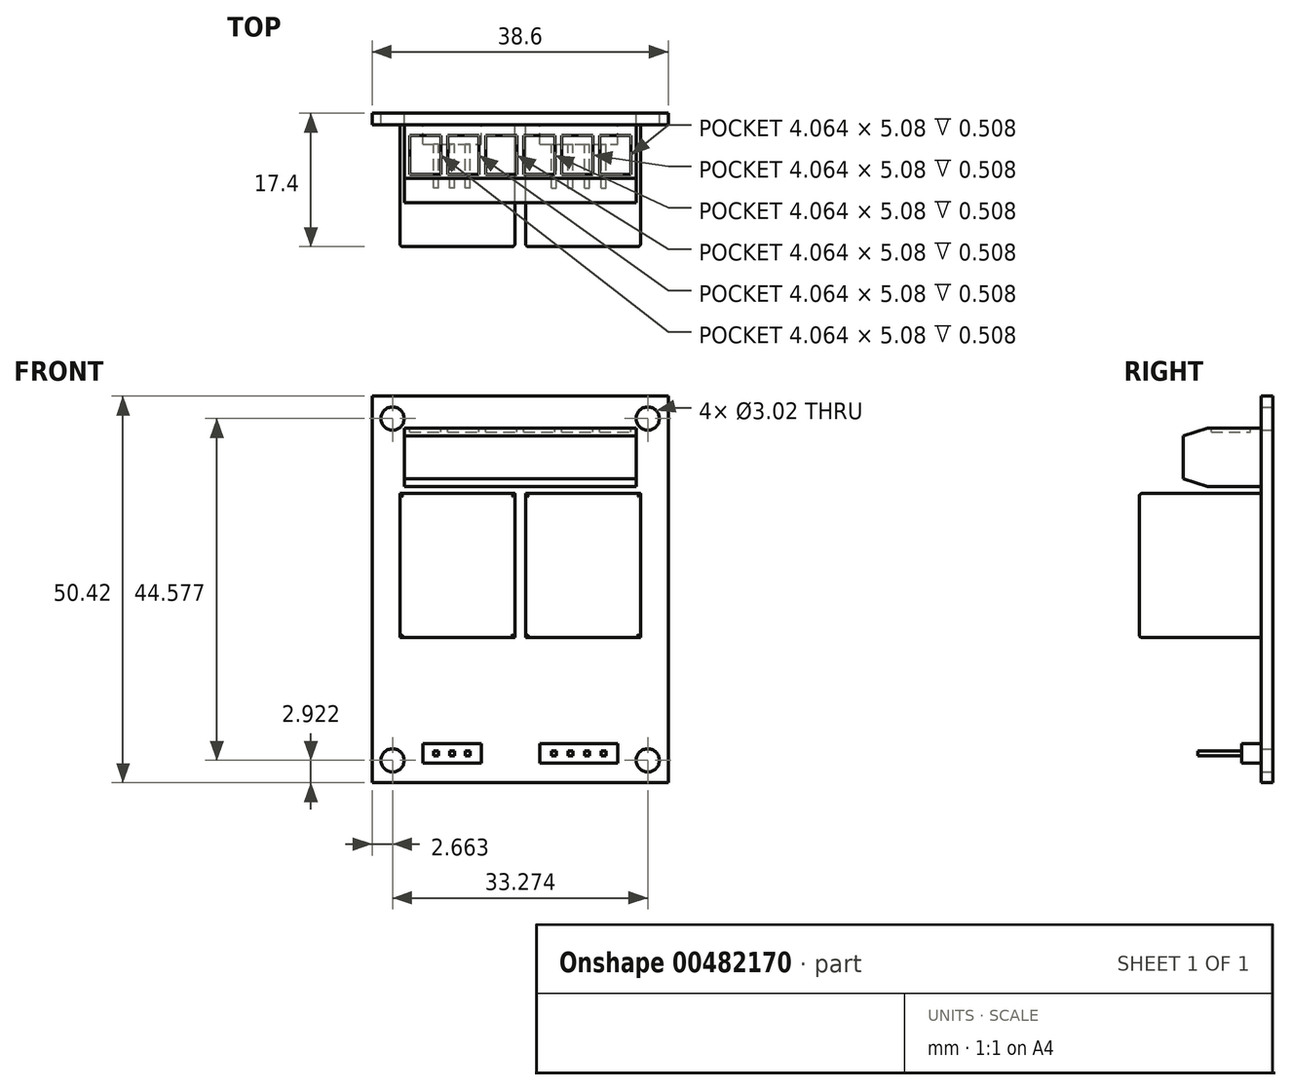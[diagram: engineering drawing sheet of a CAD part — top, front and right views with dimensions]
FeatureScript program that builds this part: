
annotation { "Feature Type Name" : "Feature", "Feature Type Description" : "" }
export const myFeature = defineFeature(function(context is Context, id is Id, definition is map)
    precondition{}
    {
        {
            var Q0;
            Q0=qCreatedBy(makeId("Front.planeOp"),FACE);
            var sketch = newSketch(context, id + "F0", { "sketchPlane" : qUnion([Q0])});
            skLineSegment(sketch, "E0.bottom", {"start": v(-19.3, 25.2) * mm, "end": v(19.3, 25.2) * mm});
            skLineSegment(sketch, "E0.top", {"start": v(-19.3, -25.2) * mm, "end": v(19.3, -25.2) * mm});
            skLineSegment(sketch, "E0.left", {"start": v(-19.3, 25.2) * mm, "end": v(-19.3, -25.2) * mm});
            skLineSegment(sketch, "E0.right", {"start": v(19.3, 25.2) * mm, "end": v(19.3, -25.2) * mm});
            skPoint(sketch, "E0.middle", {"position": v(0, 0) * mm});
            skLineSegment(sketch, "E1.bottom", {"start": v(16.64, 22.29) * mm, "end": v(-16.64, 22.29) * mm, "construction": true});
            skLineSegment(sketch, "E1.top", {"start": v(16.64, -22.29) * mm, "end": v(-16.64, -22.29) * mm, "construction": true});
            skLineSegment(sketch, "E1.left", {"start": v(16.64, 22.29) * mm, "end": v(16.64, -22.29) * mm, "construction": true});
            skLineSegment(sketch, "E1.right", {"start": v(-16.64, 22.29) * mm, "end": v(-16.64, -22.29) * mm, "construction": true});
            skCircle(sketch, "E2", {"center": v(-16.64, 22.29) * mm, "radius": 1.51 * mm});
            skCircle(sketch, "E3", {"center": v(16.64, 22.29) * mm, "radius": 1.51 * mm});
            skCircle(sketch, "E4", {"center": v(16.64, -22.29) * mm, "radius": 1.51 * mm});
            skCircle(sketch, "E5", {"center": v(-16.64, -22.29) * mm, "radius": 1.51 * mm});
            skSolve(sketch);
        }
        {
            var Q0;
            Q0 = qSketchRegion(id + "F0", true);
            extrude(context, id + "F1", {"entities" : qUnion([Q0]), "depth" : 1.52 * mm});
        }
        {
            var Q0;
            Q0=makeQuery(id+"F1.opExtrude","CAP_FACE",FACE,{"disambiguationData":[OSD([sQuery(id+"F0.wireOp",EDGE,"E0.bottom"),sQuery(id+"F0.wireOp",EDGE,"E0.top"),sQuery(id+"F0.wireOp",EDGE,"E0.left"),sQuery(id+"F0.wireOp",EDGE,"E0.right"),sQuery(id+"F0.wireOp",EDGE,"E2"),sQuery(id+"F0.wireOp",EDGE,"E3"),sQuery(id+"F0.wireOp",EDGE,"E4"),sQuery(id+"F0.wireOp",EDGE,"E5")])],"isStart":false});
            var sketch = newSketch(context, id + "F2", { "sketchPlane" : qUnion([Q0])});
            skLineSegment(sketch, "E6.bottom", {"start": v(-15.68, -6.29) * mm, "end": v(-0.7, -6.29) * mm});
            skLineSegment(sketch, "E6.top", {"start": v(-15.68, 12.5) * mm, "end": v(-0.7, 12.5) * mm});
            skLineSegment(sketch, "E6.left", {"start": v(-15.68, -6.29) * mm, "end": v(-15.68, 12.5) * mm});
            skLineSegment(sketch, "E6.right", {"start": v(-0.7, -6.29) * mm, "end": v(-0.7, 12.5) * mm});
            skLineSegment(sketch, "E7.bottom", {"start": v(0.7, -6.29) * mm, "end": v(15.68, -6.29) * mm});
            skLineSegment(sketch, "E7.top", {"start": v(0.7, 12.5) * mm, "end": v(15.68, 12.5) * mm});
            skLineSegment(sketch, "E7.left", {"start": v(0.7, -6.29) * mm, "end": v(0.7, 12.5) * mm});
            skLineSegment(sketch, "E7.right", {"start": v(15.68, -6.29) * mm, "end": v(15.68, 12.5) * mm});
            skLineSegment(sketch, "E8", {"start": v(-0.7, 0) * mm, "end": v(0.7, 0) * mm, "construction": true});
            skSolve(sketch);
        }
        {
            var Q0;
            Q0 = qSketchRegion(id + "F2", true);
            extrude(context, id + "F3", {"entities" : qUnion([Q0]), "operationType" : NewBodyOperationType.ADD, "depth" : 15.88 * mm});
        }
        {
            var Q0;
            Q0=makeQuery(id+"F3.opExtrude","CAP_FACE",FACE,{"disambiguationData":[OSD([sQuery(id+"F2.wireOp",EDGE,"E6.bottom"),sQuery(id+"F2.wireOp",EDGE,"E6.top"),sQuery(id+"F2.wireOp",EDGE,"E6.left"),sQuery(id+"F2.wireOp",EDGE,"E6.right")])],"isStart":false});
            var Q1;
            Q1=makeQuery(id+"F3.opExtrude","CAP_FACE",FACE,{"disambiguationData":[OSD([sQuery(id+"F2.wireOp",EDGE,"E7.bottom"),sQuery(id+"F2.wireOp",EDGE,"E7.top"),sQuery(id+"F2.wireOp",EDGE,"E7.left"),sQuery(id+"F2.wireOp",EDGE,"E7.right")])],"isStart":false});
            fillet(context, id + "F4", {"entities" : qUnion([Q0, Q1]), "radius" : 0.38 * mm, "tangentPropagation" : true, "allowEdgeOverflow" : false});
        }
        {
            var Q0;
            Q0=makeQuery(id+"F1.opExtrude","CAP_FACE",FACE,{"disambiguationData":[OSD([sQuery(id+"F0.wireOp",EDGE,"E0.bottom"),sQuery(id+"F0.wireOp",EDGE,"E0.top"),sQuery(id+"F0.wireOp",EDGE,"E0.left"),sQuery(id+"F0.wireOp",EDGE,"E0.right"),sQuery(id+"F0.wireOp",EDGE,"E2"),sQuery(id+"F0.wireOp",EDGE,"E3"),sQuery(id+"F0.wireOp",EDGE,"E4"),sQuery(id+"F0.wireOp",EDGE,"E5")])],"isStart":false});
            var sketch = newSketch(context, id + "F5", { "sketchPlane" : qUnion([Q0])});
            skLineSegment(sketch, "E9.bottom", {"start": v(-15.11, 13.4) * mm, "end": v(15.11, 13.4) * mm});
            skLineSegment(sketch, "E9.top", {"start": v(-15.11, 21.02) * mm, "end": v(15.11, 21.02) * mm});
            skLineSegment(sketch, "E9.left", {"start": v(-15.11, 13.4) * mm, "end": v(-15.11, 21.02) * mm});
            skLineSegment(sketch, "E9.right", {"start": v(15.11, 13.4) * mm, "end": v(15.11, 21.02) * mm});
            skLineSegment(sketch, "E10", {"start": v(0, 13.4) * mm, "end": v(0, 0) * mm, "construction": true});
            skSolve(sketch);
        }
        {
            var Q0;
            Q0 = qSketchRegion(id + "F5", true);
            extrude(context, id + "F6", {"entities" : qUnion([Q0]), "operationType" : NewBodyOperationType.ADD, "depth" : 10.16 * mm});
        }
        {
            var Q0;
            Q0=makeQuery(id+"F6.opExtrude","CAP_EDGE",EDGE,{"disambiguationData":[OSD([sQuery(id+"F5.wireOp",EDGE,"E9.top")])],"isStart":false});
            var Q1;
            Q1=makeQuery(id+"F6.opExtrude","CAP_EDGE",EDGE,{"disambiguationData":[OSD([sQuery(id+"F5.wireOp",EDGE,"E9.bottom")])],"isStart":false});
            chamfer(context, id + "F7", {"entities" : qUnion([Q0, Q1]), "chamferType" : ChamferType.TWO_OFFSETS, "width1" : 3.17 * mm, "oppositeDirection" : false, "width2" : 1.02 * mm, "tangentPropagation" : true});
        }
        {
            var Q0;
            Q0=makeQuery(id+"F6.opExtrude","SWEPT_FACE",FACE,{"disambiguationData":[OSD([sQuery(id+"F5.wireOp",EDGE,"E9.top")])]});
            var sketch = newSketch(context, id + "F8", { "sketchPlane" : qUnion([Q0])});
            skLineSegment(sketch, "E11.bottom", {"start": v(-14.41, -8) * mm, "end": v(-10.35, -8) * mm});
            skLineSegment(sketch, "E11.top", {"start": v(-14.41, -2.92) * mm, "end": v(-10.35, -2.92) * mm});
            skLineSegment(sketch, "E11.left", {"start": v(-14.41, -8) * mm, "end": v(-14.41, -2.92) * mm});
            skLineSegment(sketch, "E11.right", {"start": v(-10.35, -8) * mm, "end": v(-10.35, -2.92) * mm});
            skLineSegment(sketch, "E12.bottom", {"start": v(-9.46, -8) * mm, "end": v(-5.4, -8) * mm});
            skLineSegment(sketch, "E12.top", {"start": v(-9.46, -2.92) * mm, "end": v(-5.4, -2.92) * mm});
            skLineSegment(sketch, "E12.left", {"start": v(-9.46, -8) * mm, "end": v(-9.46, -2.92) * mm});
            skLineSegment(sketch, "E12.right", {"start": v(-5.4, -8) * mm, "end": v(-5.4, -2.92) * mm});
            skLineSegment(sketch, "E13.bottom", {"start": v(-4.5, -8) * mm, "end": v(-0.44, -8) * mm});
            skLineSegment(sketch, "E13.top", {"start": v(-4.5, -2.92) * mm, "end": v(-0.44, -2.92) * mm});
            skLineSegment(sketch, "E13.left", {"start": v(-4.5, -8) * mm, "end": v(-4.5, -2.92) * mm});
            skLineSegment(sketch, "E13.right", {"start": v(-0.44, -8) * mm, "end": v(-0.44, -2.92) * mm});
            skLineSegment(sketch, "E14", {"start": v(-10.35, -2.92) * mm, "end": v(-9.46, -2.92) * mm, "construction": true});
            skLineSegment(sketch, "E15", {"start": v(-5.4, -2.92) * mm, "end": v(-4.5, -2.92) * mm, "construction": true});
            skLineSegment(sketch, "E16.bottom", {"start": v(0.44, -8) * mm, "end": v(4.5, -8) * mm});
            skLineSegment(sketch, "E16.top", {"start": v(0.44, -2.92) * mm, "end": v(4.5, -2.92) * mm});
            skLineSegment(sketch, "E16.left", {"start": v(0.44, -8) * mm, "end": v(0.44, -2.92) * mm});
            skLineSegment(sketch, "E16.right", {"start": v(4.5, -8) * mm, "end": v(4.5, -2.92) * mm});
            skLineSegment(sketch, "E17.bottom", {"start": v(5.4, -8) * mm, "end": v(9.46, -8) * mm});
            skLineSegment(sketch, "E17.top", {"start": v(5.4, -2.92) * mm, "end": v(9.46, -2.92) * mm});
            skLineSegment(sketch, "E17.left", {"start": v(5.4, -8) * mm, "end": v(5.4, -2.92) * mm});
            skLineSegment(sketch, "E17.right", {"start": v(9.46, -8) * mm, "end": v(9.46, -2.92) * mm});
            skLineSegment(sketch, "E18.bottom", {"start": v(10.35, -8) * mm, "end": v(14.41, -8) * mm});
            skLineSegment(sketch, "E18.top", {"start": v(10.35, -2.92) * mm, "end": v(14.41, -2.92) * mm});
            skLineSegment(sketch, "E18.left", {"start": v(10.35, -8) * mm, "end": v(10.35, -2.92) * mm});
            skLineSegment(sketch, "E18.right", {"start": v(14.41, -8) * mm, "end": v(14.41, -2.92) * mm});
            skLineSegment(sketch, "E19", {"start": v(-0.44, -2.92) * mm, "end": v(0.44, -2.92) * mm, "construction": true});
            skLineSegment(sketch, "E20", {"start": v(4.5, -2.92) * mm, "end": v(5.4, -2.92) * mm, "construction": true});
            skLineSegment(sketch, "E21", {"start": v(9.46, -2.92) * mm, "end": v(10.35, -2.92) * mm, "construction": true});
            skLineSegment(sketch, "E22", {"start": v(-14.41, -8) * mm, "end": v(-15.11, -8) * mm, "construction": true});
            skLineSegment(sketch, "E23", {"start": v(14.41, -8) * mm, "end": v(15.11, -8) * mm, "construction": true});
            skSolve(sketch);
        }
        {
            var Q0;
            Q0 = qSketchRegion(id + "F8", true);
            extrude(context, id + "F9", {"entities" : qUnion([Q0]), "operationType" : NewBodyOperationType.REMOVE, "oppositeDirection" : true, "depth" : 0.5 * mm});
        }
        {
            var Q0;
            Q0=makeQuery(id+"F1.opExtrude","CAP_FACE",FACE,{"disambiguationData":[OSD([sQuery(id+"F0.wireOp",EDGE,"E0.bottom"),sQuery(id+"F0.wireOp",EDGE,"E0.top"),sQuery(id+"F0.wireOp",EDGE,"E0.left"),sQuery(id+"F0.wireOp",EDGE,"E0.right"),sQuery(id+"F0.wireOp",EDGE,"E2"),sQuery(id+"F0.wireOp",EDGE,"E3"),sQuery(id+"F0.wireOp",EDGE,"E4"),sQuery(id+"F0.wireOp",EDGE,"E5")])],"isStart":false});
            var sketch = newSketch(context, id + "F10", { "sketchPlane" : qUnion([Q0])});
            skLineSegment(sketch, "E24.bottom", {"start": v(-12.7, -22.67) * mm, "end": v(-5.08, -22.67) * mm});
            skLineSegment(sketch, "E24.top", {"start": v(-12.7, -20.13) * mm, "end": v(-5.08, -20.13) * mm});
            skLineSegment(sketch, "E24.left", {"start": v(-12.7, -22.67) * mm, "end": v(-12.7, -20.13) * mm});
            skLineSegment(sketch, "E24.right", {"start": v(-5.08, -22.67) * mm, "end": v(-5.08, -20.13) * mm});
            skLineSegment(sketch, "E25.bottom", {"start": v(2.54, -22.67) * mm, "end": v(12.7, -22.67) * mm});
            skLineSegment(sketch, "E25.top", {"start": v(2.54, -20.13) * mm, "end": v(12.7, -20.13) * mm});
            skLineSegment(sketch, "E25.left", {"start": v(2.54, -22.67) * mm, "end": v(2.54, -20.13) * mm});
            skLineSegment(sketch, "E25.right", {"start": v(12.7, -22.67) * mm, "end": v(12.7, -20.13) * mm});
            skSolve(sketch);
        }
        {
            var Q0;
            Q0 = qSketchRegion(id + "F10", true);
            extrude(context, id + "F11", {"entities" : qUnion([Q0]), "operationType" : NewBodyOperationType.ADD, "depth" : 2.54 * mm});
        }
        {
            var Q0;
            Q0=makeQuery(id+"F11.opExtrude","CAP_FACE",FACE,{"disambiguationData":[OSD([sQuery(id+"F10.wireOp",EDGE,"E25.bottom"),sQuery(id+"F10.wireOp",EDGE,"E25.top"),sQuery(id+"F10.wireOp",EDGE,"E25.left"),sQuery(id+"F10.wireOp",EDGE,"E25.right")])],"isStart":false});
            var sketch = newSketch(context, id + "F12", { "sketchPlane" : qUnion([Q0])});
            skLineSegment(sketch, "E26.bottom", {"start": v(4.06, -21.72) * mm, "end": v(4.7, -21.72) * mm});
            skLineSegment(sketch, "E26.top", {"start": v(4.06, -21.08) * mm, "end": v(4.7, -21.08) * mm});
            skLineSegment(sketch, "E26.left", {"start": v(4.06, -21.72) * mm, "end": v(4.06, -21.08) * mm});
            skLineSegment(sketch, "E26.right", {"start": v(4.7, -21.72) * mm, "end": v(4.7, -21.08) * mm});
            skLineSegment(sketch, "E27.bottom", {"start": v(6.22, -21.72) * mm, "end": v(6.86, -21.72) * mm});
            skLineSegment(sketch, "E27.top", {"start": v(6.22, -21.08) * mm, "end": v(6.86, -21.08) * mm});
            skLineSegment(sketch, "E27.left", {"start": v(6.22, -21.72) * mm, "end": v(6.22, -21.08) * mm});
            skLineSegment(sketch, "E27.right", {"start": v(6.86, -21.72) * mm, "end": v(6.86, -21.08) * mm});
            skLineSegment(sketch, "E28.bottom", {"start": v(8.38, -21.72) * mm, "end": v(9.02, -21.72) * mm});
            skLineSegment(sketch, "E28.top", {"start": v(8.38, -21.08) * mm, "end": v(9.02, -21.08) * mm});
            skLineSegment(sketch, "E28.left", {"start": v(8.38, -21.72) * mm, "end": v(8.38, -21.08) * mm});
            skLineSegment(sketch, "E28.right", {"start": v(9.02, -21.72) * mm, "end": v(9.02, -21.08) * mm});
            skLineSegment(sketch, "E29.bottom", {"start": v(10.54, -21.72) * mm, "end": v(11.18, -21.72) * mm});
            skLineSegment(sketch, "E29.top", {"start": v(10.54, -21.08) * mm, "end": v(11.18, -21.08) * mm});
            skLineSegment(sketch, "E29.left", {"start": v(10.54, -21.72) * mm, "end": v(10.54, -21.08) * mm});
            skLineSegment(sketch, "E29.right", {"start": v(11.18, -21.72) * mm, "end": v(11.18, -21.08) * mm});
            skLineSegment(sketch, "E30", {"start": v(2.54, -21.4) * mm, "end": v(4.06, -21.4) * mm, "construction": true});
            skLineSegment(sketch, "E31", {"start": v(4.7, -21.4) * mm, "end": v(6.22, -21.4) * mm, "construction": true});
            skLineSegment(sketch, "E32", {"start": v(11.18, -21.4) * mm, "end": v(12.7, -21.4) * mm, "construction": true});
            skLineSegment(sketch, "E33", {"start": v(6.86, -21.4) * mm, "end": v(8.38, -21.4) * mm, "construction": true});
            skLineSegment(sketch, "E34", {"start": v(9.02, -21.4) * mm, "end": v(10.54, -21.4) * mm, "construction": true});
            skLineSegment(sketch, "E35.bottom", {"start": v(-6.5, -21.72) * mm, "end": v(-7.14, -21.72) * mm});
            skLineSegment(sketch, "E35.top", {"start": v(-6.5, -21.08) * mm, "end": v(-7.14, -21.08) * mm});
            skLineSegment(sketch, "E35.left", {"start": v(-6.5, -21.72) * mm, "end": v(-6.5, -21.08) * mm});
            skLineSegment(sketch, "E35.right", {"start": v(-7.14, -21.72) * mm, "end": v(-7.14, -21.08) * mm});
            skLineSegment(sketch, "E36.bottom", {"start": v(-8.57, -21.72) * mm, "end": v(-9.2, -21.72) * mm});
            skLineSegment(sketch, "E36.top", {"start": v(-8.57, -21.08) * mm, "end": v(-9.2, -21.08) * mm});
            skLineSegment(sketch, "E36.left", {"start": v(-8.57, -21.72) * mm, "end": v(-8.57, -21.08) * mm});
            skLineSegment(sketch, "E36.right", {"start": v(-9.2, -21.72) * mm, "end": v(-9.2, -21.08) * mm});
            skLineSegment(sketch, "E37.bottom", {"start": v(-10.64, -21.72) * mm, "end": v(-11.27, -21.72) * mm});
            skLineSegment(sketch, "E37.top", {"start": v(-10.64, -21.08) * mm, "end": v(-11.27, -21.08) * mm});
            skLineSegment(sketch, "E37.left", {"start": v(-10.64, -21.72) * mm, "end": v(-10.64, -21.08) * mm});
            skLineSegment(sketch, "E37.right", {"start": v(-11.27, -21.72) * mm, "end": v(-11.27, -21.08) * mm});
            skLineSegment(sketch, "E38", {"start": v(-8.57, -21.4) * mm, "end": v(-7.14, -21.4) * mm, "construction": true});
            skLineSegment(sketch, "E39", {"start": v(-9.2, -21.4) * mm, "end": v(-10.64, -21.4) * mm, "construction": true});
            skLineSegment(sketch, "E40", {"start": v(-11.27, -21.4) * mm, "end": v(-12.7, -21.4) * mm, "construction": true});
            skLineSegment(sketch, "E41", {"start": v(-6.5, -21.4) * mm, "end": v(-5.08, -21.4) * mm, "construction": true});
            skSolve(sketch);
        }
        {
            var Q0;
            Q0 = qSketchRegion(id + "F12", true);
            extrude(context, id + "F13", {"entities" : qUnion([Q0]), "operationType" : NewBodyOperationType.ADD, "depth" : 5.7 * mm});
        }
    });
